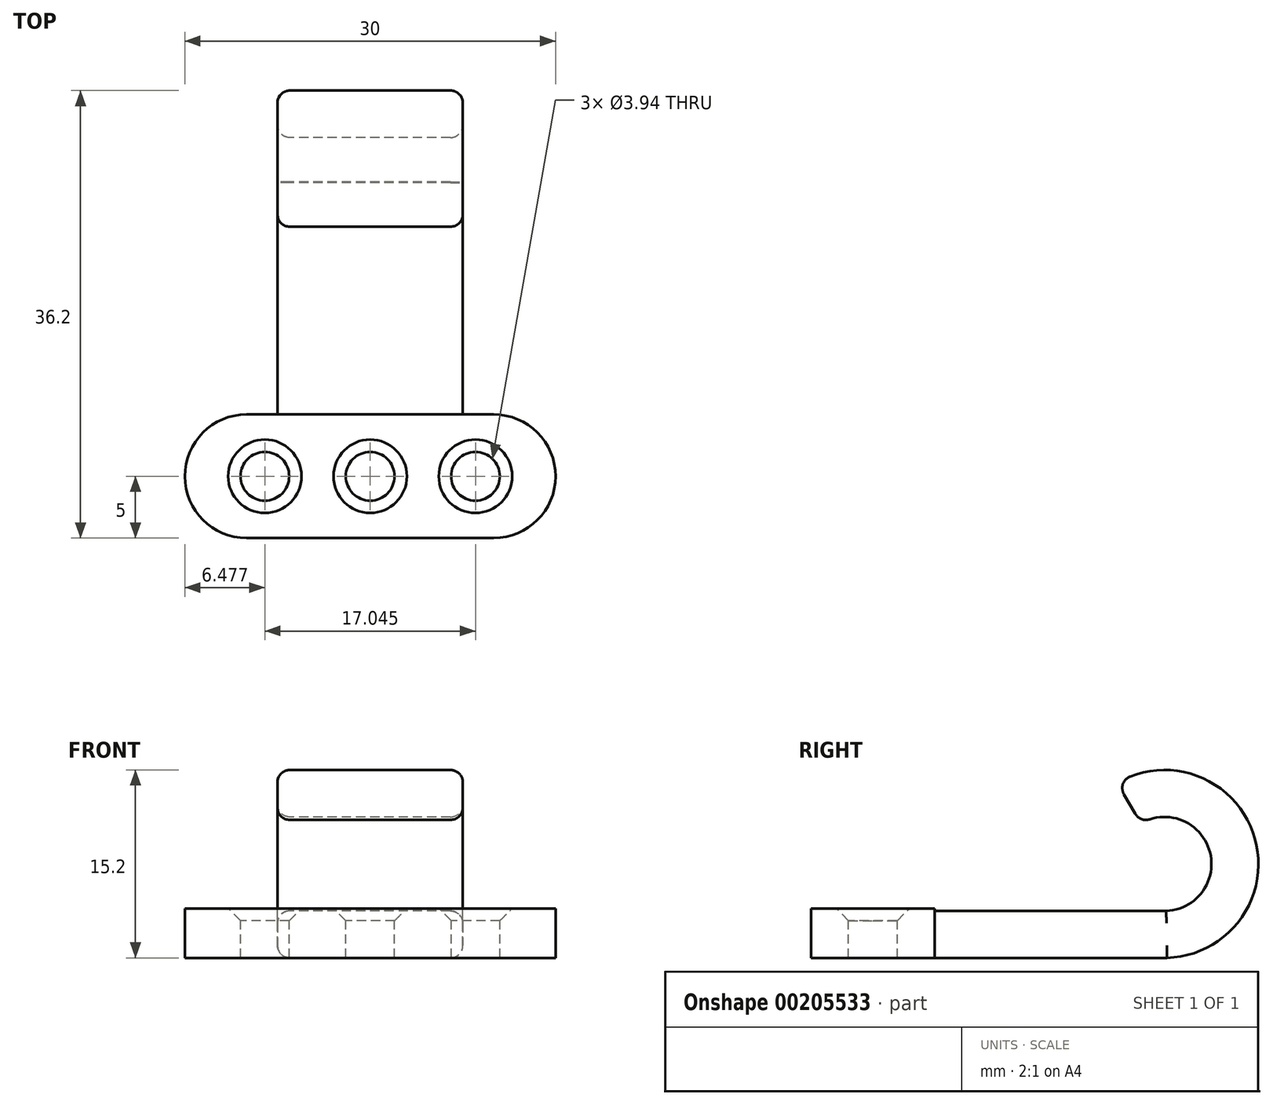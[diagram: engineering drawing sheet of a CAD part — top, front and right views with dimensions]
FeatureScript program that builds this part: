
annotation { "Feature Type Name" : "Feature", "Feature Type Description" : "" }
export const myFeature = defineFeature(function(context is Context, id is Id, definition is map)
    precondition{}
    {
        {
            var Q0;
            Q0=qCreatedBy(makeId("Right.planeOp"),FACE);
            var sketch = newSketch(context, id + "F0", { "sketchPlane" : qUnion([Q0])});
            skLineSegment(sketch, "E0.bottom", {"start": v(-5, 2) * mm, "end": v(5, 2) * mm});
            skLineSegment(sketch, "E0.top", {"start": v(-5, -2) * mm, "end": v(5, -2) * mm});
            skLineSegment(sketch, "E0.left", {"start": v(-5, 2) * mm, "end": v(-5, -2) * mm});
            skLineSegment(sketch, "E0.right", {"start": v(5, 2) * mm, "end": v(5, -2) * mm});
            skPoint(sketch, "E0.middle", {"position": v(0, 0) * mm});
            skLineSegment(sketch, "E1.bottom", {"start": v(5, -2) * mm, "end": v(23.8, -2) * mm});
            skLineSegment(sketch, "E1.top", {"start": v(5, 1.8) * mm, "end": v(23.8, 1.8) * mm});
            skLineSegment(sketch, "E1.left", {"start": v(5, -2) * mm, "end": v(5, 1.8) * mm});
            skLineSegment(sketch, "E1.right", {"start": v(23.8, -2) * mm, "end": v(23.8, 1.8) * mm});
            skArc(sketch, "E2", {"start": v(23.8, -2) * mm, "mid": v(30.91, 7.67) * mm, "end": v(19.78, 12.17) * mm});
            skArc(sketch, "E3.0", {"start": v(23.7, 1.8) * mm, "mid": v(27.25, 6.63) * mm, "end": v(21.7, 8.88) * mm});
            skLineSegment(sketch, "E4", {"start": v(19.78, 12.17) * mm, "end": v(21.7, 8.88) * mm});
            skSolve(sketch);
        }
        {
            var Q0;
            Q0=makeQuery(id+"F0.imprint","IMPRINT",FACE,{"disambiguationData":[TD([[makeQuery(id+"F0.imprint","IMPRINT",EDGE,{"derivedFrom":sQuery(id+"F0.wireOp",EDGE,"E0.bottom")}),-1.0]])]});
            extrude(context, id + "F1", {"entities" : qUnion([Q0]), "endBound" : BoundingType.SYMMETRIC, "depth" : 30 * mm});
        }
        {
            var Q0;
            Q0=makeQuery(id+"F0.imprint","IMPRINT",FACE,{"disambiguationData":[TD([[makeQuery(id+"F0.imprint","IMPRINT",EDGE,{"derivedFrom":sQuery(id+"F0.wireOp",EDGE,"E1.bottom")}),1.0]])]});
            var Q1;
            {var subQ4=sQuery(id+"F0.wireOp",EDGE,"E1.right");Q1=makeQuery(id+"F0.imprint","IMPRINT",FACE,{"disambiguationData":[TD([[makeQuery(id+"F0.imprint","IMPRINT",EDGE,{"derivedFrom":subQ4}),-1.0]])]});}
            extrude(context, id + "F2", {"entities" : qUnion([Q0, Q1]), "operationType" : NewBodyOperationType.ADD, "endBound" : BoundingType.SYMMETRIC, "depth" : 15 * mm});
        }
        {
            var Q0;
            Q0=qCreatedBy(makeId("Top.planeOp"),FACE);
            var sketch = newSketch(context, id + "F3", { "sketchPlane" : qUnion([Q0])});
            skCircle(sketch, "E5", {"center": v(0, 0) * mm, "radius": 1.97 * mm});
            skCircle(sketch, "E6", {"center": v(-8.52, 0) * mm, "radius": 1.97 * mm});
            skCircle(sketch, "E7.MirrorC", {"center": v(8.52, 0) * mm, "radius": 1.97 * mm});
            skSolve(sketch);
        }
        {
            var Q0;
            Q0 = qSketchRegion(id + "F3", true);
            extrude(context, id + "F4", {"entities" : qUnion([Q0]), "operationType" : NewBodyOperationType.REMOVE, "endBound" : BoundingType.SYMMETRIC, "oppositeDirection" : true, "depth" : 25 * mm});
        }
        {
            var Q0;
            Q0=makeQuery(id+"F1.opExtrude","CAP_EDGE",EDGE,{"disambiguationData":[OSD([sQuery(id+"F0.wireOp",EDGE,"E0.left")])],"isStart":true});
            var Q1;
            Q1=makeQuery(id+"F1.opExtrude","CAP_EDGE",EDGE,{"disambiguationData":[OSD([sQuery(id+"F0.wireOp",EDGE,"E0.right"),sQuery(id+"F0.wireOp",EDGE,"E1.left")])],"isStart":true});
            var Q2;
            Q2=makeQuery(id+"F1.opExtrude","CAP_EDGE",EDGE,{"disambiguationData":[OSD([sQuery(id+"F0.wireOp",EDGE,"E0.left")])],"isStart":false});
            var Q3;
            Q3=makeQuery(id+"F1.opExtrude","CAP_EDGE",EDGE,{"disambiguationData":[OSD([sQuery(id+"F0.wireOp",EDGE,"E0.right"),sQuery(id+"F0.wireOp",EDGE,"E1.left")])],"isStart":false});
            fillet(context, id + "F5", {"entities" : qUnion([Q0, Q1, Q2, Q3]), "radius" : 5 * mm, "tangentPropagation" : true, "allowEdgeOverflow" : false});
        }
        {
            var Q0;
            Q0=makeQuery(id+"F4.boolean.opBoolean","INTERSECT",EDGE,{"derivedFrom":[makeQuery(id+"F1.opExtrude","SWEPT_FACE",FACE,{"disambiguationData":[OSD([sQuery(id+"F0.wireOp",EDGE,"E0.bottom")])]}),makeQuery(id+"F4.opExtrude","SWEPT_FACE",FACE,{"disambiguationData":[OSD([sQuery(id+"F3.wireOp",EDGE,"E6")])]})]});
            var Q1;
            Q1=makeQuery(id+"F4.boolean.opBoolean","INTERSECT",EDGE,{"derivedFrom":[makeQuery(id+"F1.opExtrude","SWEPT_FACE",FACE,{"disambiguationData":[OSD([sQuery(id+"F0.wireOp",EDGE,"E0.bottom")])]}),makeQuery(id+"F4.opExtrude","SWEPT_FACE",FACE,{"disambiguationData":[OSD([sQuery(id+"F3.wireOp",EDGE,"E5")])]})]});
            var Q2;
            Q2=makeQuery(id+"F4.boolean.opBoolean","INTERSECT",EDGE,{"derivedFrom":[makeQuery(id+"F1.opExtrude","SWEPT_FACE",FACE,{"disambiguationData":[OSD([sQuery(id+"F0.wireOp",EDGE,"E0.bottom")])]}),makeQuery(id+"F4.opExtrude","SWEPT_FACE",FACE,{"disambiguationData":[OSD([sQuery(id+"F3.wireOp",EDGE,"E7.MirrorC")])]})]});
            chamfer(context, id + "F6", {"entities" : qUnion([Q0, Q1, Q2]), "width" : 1 * mm, "tangentPropagation" : true});
        }
        {
            var Q0;
            Q0=makeQuery(id+"F2.opExtrude","CAP_EDGE",EDGE,{"disambiguationData":[OSD([sQuery(id+"F0.wireOp",EDGE,"E1.top")])],"isStart":false});
            var Q1;
            Q1=makeQuery(id+"F2.opExtrude","CAP_EDGE",EDGE,{"disambiguationData":[OSD([sQuery(id+"F0.wireOp",EDGE,"E1.top")])],"isStart":true});
            var Q2;
            Q2=makeQuery(id+"F2.opExtrude","CAP_EDGE",EDGE,{"disambiguationData":[OSD([sQuery(id+"F0.wireOp",EDGE,"E3.0")])],"isStart":false});
            var Q3;
            Q3=makeQuery(id+"F2.opExtrude","CAP_EDGE",EDGE,{"disambiguationData":[OSD([sQuery(id+"F0.wireOp",EDGE,"E3.0")])],"isStart":true});
            var Q4;
            Q4=makeQuery(id+"F2.opExtrude","SWEPT_EDGE",EDGE,{"disambiguationData":[OSD([sQuery(id+"F0.wireOp",EDGE,"E3.0"),sQuery(id+"F0.wireOp",EDGE,"E4")])]});
            var Q5;
            Q5=makeQuery(id+"F2.opExtrude","SWEPT_EDGE",EDGE,{"disambiguationData":[OSD([sQuery(id+"F0.wireOp",EDGE,"E2"),sQuery(id+"F0.wireOp",EDGE,"E4")])]});
            var Q6;
            Q6=makeQuery(id+"F2.opExtrude","CAP_EDGE",EDGE,{"disambiguationData":[OSD([sQuery(id+"F0.wireOp",EDGE,"E4")])],"isStart":false});
            var Q7;
            Q7=makeQuery(id+"F2.opExtrude","CAP_EDGE",EDGE,{"disambiguationData":[OSD([sQuery(id+"F0.wireOp",EDGE,"E4")])],"isStart":true});
            var Q8;
            Q8=makeQuery(id+"F2.opExtrude","CAP_EDGE",EDGE,{"disambiguationData":[OSD([sQuery(id+"F0.wireOp",EDGE,"E2")])],"isStart":false});
            var Q9;
            Q9=makeQuery(id+"F2.opExtrude","CAP_EDGE",EDGE,{"disambiguationData":[OSD([sQuery(id+"F0.wireOp",EDGE,"E2")])],"isStart":true});
            var Q10;
            Q10=makeQuery(id+"F2.opExtrude","CAP_EDGE",EDGE,{"disambiguationData":[OSD([sQuery(id+"F0.wireOp",EDGE,"E1.bottom")])],"isStart":false});
            var Q11;
            Q11=makeQuery(id+"F2.opExtrude","CAP_EDGE",EDGE,{"disambiguationData":[OSD([sQuery(id+"F0.wireOp",EDGE,"E1.bottom")])],"isStart":true});
            fillet(context, id + "F7", {"entities" : qUnion([Q0, Q1, Q2, Q3, Q4, Q5, Q6, Q7, Q8, Q9, Q10, Q11]), "radius" : 1 * mm, "allowEdgeOverflow" : false});
        }
    });
